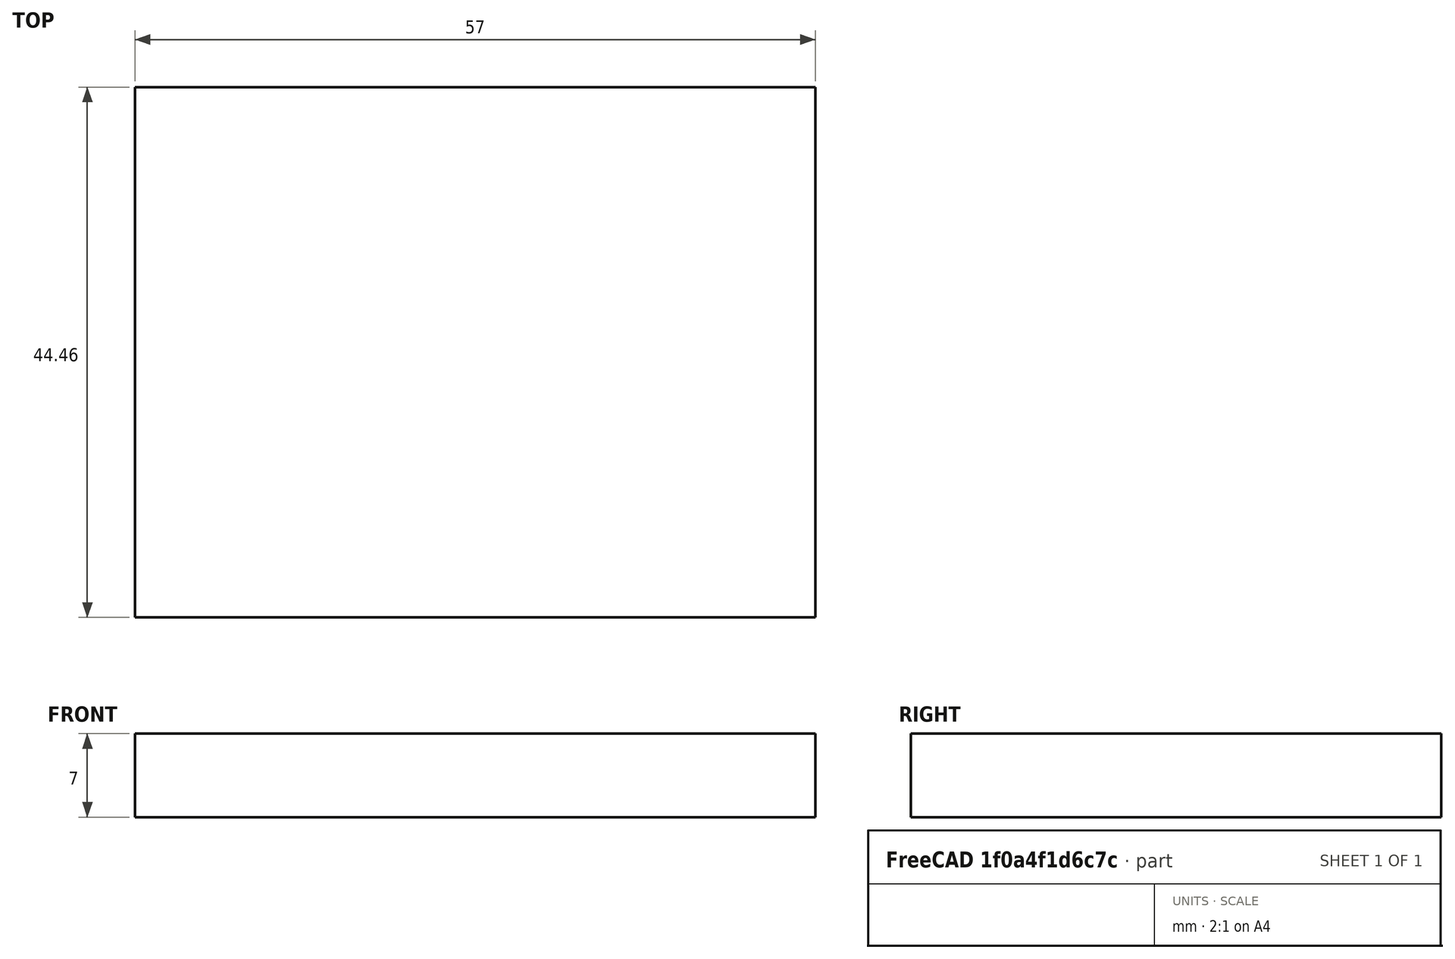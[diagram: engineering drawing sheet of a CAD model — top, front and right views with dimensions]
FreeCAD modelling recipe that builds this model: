
FCSTD DOCUMENT  (FreeCAD 0.17RUnknown)
Label: cam_cage
License: All rights reserved
LicenseURL: http://en.wikipedia.org/wiki/All_rights_reserved
objects: Path::FeaturePython×8, Part::FeaturePython×3, App::FeaturePython×1, Path::FeatureCompoundPython×1
note: 6 computed .brp shape members not serialized (recipe doc carries the construction recipe); baked Part::Feature solids carry a one-line shape summary decoded from their .brp

FEATURE [Path::FeaturePython] Default_Tool  label="Default Tool"  # Path/CAM operation (typed FeaturePython)
  HorizFeed = 3.33333
  HorizRapid = 0
  SpindleDir = 0
  SpindleSpeed = 24000
  ToolNumber = 1
  VertFeed = 0.666667
  VertRapid = 0
  expr: Tool.Diameter = 2
  expr: VertFeed = 40mm / min
  expr: HorizFeed = 200mm / min
  expr: HorizRapid = SetupSheet.HorizRapid
  expr: VertRapid = SetupSheet.VertRapid
FEATURE [Path::FeaturePython] Contour  # Path/CAM operation (typed FeaturePython)
  Active = true
  AreaParams:
    OpenMode = 0
    Angle = 45.0
    MinArcPoints = 4
    Coplanar = 2
    Tolerance = 1e-07
    CleanDistance = 0.0
    PocketExtraOffset = 0.0
    RoundPrecision = 0.0
    AngleShift = 0.0
    SubjectFill = 0
    PocketMode = 0
    Simplify = False
    SectionTolerance = 1e-06
    MaxArcPoints = 100
    Offset = 1.0
    Accuracy = 0.01
    PocketStepover = 0.0
    ClipFill = 0
    ToolRadius = 1.0
    Outline = False
    ClipperScale = 10000000.0
    FromCenter = False
    Explode = False
    EndType = 0
    Shift = 0.0
    ExtraPass = 0
    Project = False
    JoinType = 0
    Thicken = False
    Stepdown = 1.0
    SectionMode = 2
    MiterLimit = 2.0
    Deflection = 0.01
    Reorient = True
    FitArcs = True
    SectionCount = -1
    SectionOffset = 0.0
    Stepover = 0.0
    Unit = 1.0
    Fill = 0
  ClearanceHeight = 2
  Direction = 0
  FinalDepth = -5.5
  JoinType = 0
  MiterLimit = 0.1
  OffsetExtra = 0
  OpFinalDepth = -6
  OpStartDepth = 1
  OpToolDiameter = 2
  PathParams = {'resume_height': 2.0, 'feedrate': 3.3333333333333335, 'verbose': True, 'orientation': 1, 'return_end': True, 'preamble': False, 'retraction': 2.0, 'feedrate_v': 0.6666666666666666}
  SafeHeight = 2
  Side = 0
  StartDepth = 0
  StartPoint = (0,0,0)
  StepDown = 0.1
  ToolController = -> Default_Tool
  UseComp = true
  UseStartPoint = false
  expr: FinalDepth = -5.5
  expr: ClearanceHeight = StartDepth + SetupSheet.ClearanceHeightOffset
  expr: SafeHeight = StartDepth + SetupSheet.SafeHeightOffset
  expr: StepDown = 0.10000000000000001
  expr: StartDepth = 0
FEATURE [App::FeaturePython] SetupSheet  # Path/CAM operation (typed FeaturePython)
  ClearanceHeightExpression = StartDepth+SetupSheet.ClearanceHeightOffset
  ClearanceHeightOffset = 2
  FinalDepthExpression = OpFinalDepth
  HorizRapid = 0
  SafeHeightExpression = StartDepth+SetupSheet.SafeHeightOffset
  SafeHeightOffset = 2
  StartDepthExpression = OpStartDepth
  StepDownExpression = OpToolDiameter
  VertRapid = 0
FEATURE [Part::FeaturePython] cage_01  # a2plus imported part (geometry in sourceFile) (typed FeaturePython)
  Placement = pos=(-28.7964,26.9328,-28.4564) rot=(0.57735,0.57735,0.57735;0rad)
  fixedPosition = false
  sourceFile = <userpath>/hs/fly/cad/cage.fcstd
  timeLastImport = 1.53702e+09
  updateColors = true
FEATURE [Part::FeaturePython] Clone  label="Base-arm_01"  # Draft clone (typed FeaturePython)
  AttacherType = Attacher::AttachEngine3D
  Fuse = false
  Objects = -> [cage_01]
  PathResource = Base
  Placement = pos=(51,12,-2.5) rot=(-1,0,0;0rad)
  Scale = (1,1,1)
FEATURE [Part::FeaturePython] Stock  # WARN: FeaturePython — macro-defined, semantics opaque (R4)
  Base = -> Clone
  ExtXneg = 1
  ExtXpos = 1
  ExtYneg = 1
  ExtYpos = 1
  ExtZneg = 1
  ExtZpos = 1
  StockType = FromBase
FEATURE [Path::FeaturePython] Pocket_Shape001  # Path/CAM operation (typed FeaturePython)
  Active = true
  AreaParams:
    OpenMode = 0
    Angle = 45.0
    MinArcPoints = 4
    Coplanar = 0
    Tolerance = 1e-07
    CleanDistance = 0.0
    PocketExtraOffset = 0.0
    RoundPrecision = 0.0
    AngleShift = 0.0
    SubjectFill = 0
    PocketMode = 2
    Simplify = False
    SectionTolerance = 1e-06
    MaxArcPoints = 100
    Offset = 0.0
    Accuracy = 0.01
    PocketStepover = 1.0
    ClipFill = 0
    ToolRadius = 1.0
    Outline = False
    ClipperScale = 10000000.0
    FromCenter = True
    Explode = False
    EndType = 0
    Shift = 0.0
    ExtraPass = 0
    Project = False
    JoinType = 0
    Thicken = False
    Stepdown = 1.0
    SectionMode = 2
    MiterLimit = 2.0
    Deflection = 0.01
    Reorient = True
    FitArcs = True
    SectionCount = -1
    SectionOffset = 0.0
    Stepover = 0.0
    Unit = 1.0
    Fill = 0
  Base = -> [Clone]
  ClearanceHeight = 2
  CutMode = 0
  ExtraOffset = 0
  FinalDepth = -5.5
  FinishDepth = 0
  KeepToolDown = false
  MinTravel = false
  OffsetPattern = 1
  OpFinalDepth = -5
  OpStartDepth = 1
  OpToolDiameter = 2
  PathParams = {'resume_height': 2.0, 'feedrate': 3.3333333333333335, 'verbose': True, 'orientation': 1, 'return_end': True, 'preamble': False, 'retraction': 2.0, 'feedrate_v': 0.6666666666666666}
  SafeHeight = 2
  StartAt = 0
  StartDepth = 0
  StartPoint = (0,0,0)
  StepDown = 0.21
  StepOver = 50
  ToolController = -> Default_Tool
  UseStartPoint = false
  ZigZagAngle = 45
  expr: ClearanceHeight = StartDepth + SetupSheet.ClearanceHeightOffset
  expr: SafeHeight = StartDepth + SetupSheet.SafeHeightOffset
  expr: StepDown = 0.20999999999999999
  expr: FinalDepth = -5.5
  expr: StartDepth = 0
FEATURE [Path::FeaturePython] Drilling  # Path/CAM operation (typed FeaturePython)
  Active = true
  AddTipLength = false
  Base = -> [Clone]
  ClearanceHeight = 3
  Disabled = Clone.Face44 | Clone.Face45
  DwellEnabled = false
  DwellTime = 0
  FinalDepth = -0.2
  OpFinalDepth = -5
  OpStartDepth = 1
  OpToolDiameter = 2
  PeckDepth = 0
  PeckEnabled = false
  RetractHeight = 10
  ReturnLevel = 0
  SafeHeight = 3
  StartDepth = 1
  ToolController = -> Default_Tool
  expr: ClearanceHeight = StartDepth + SetupSheet.ClearanceHeightOffset
  expr: SafeHeight = StartDepth + SetupSheet.SafeHeightOffset
  expr: FinalDepth = -0.20000000000000001
  expr: StartDepth = OpStartDepth
FEATURE [Path::FeaturePython] Profile_Edges  # Path/CAM operation (typed FeaturePython)
  Active = true
  AreaParams:
    OpenMode = 0
    Angle = 45.0
    MinArcPoints = 4
    Coplanar = 0
    Tolerance = 1e-07
    CleanDistance = 0.0
    PocketExtraOffset = 0.0
    RoundPrecision = 0.0
    AngleShift = 0.0
    SubjectFill = 0
    PocketMode = 0
    Simplify = False
    SectionTolerance = 1e-06
    MaxArcPoints = 100
    Offset = -1.0
    Accuracy = 0.01
    PocketStepover = 0.0
    ClipFill = 0
    ToolRadius = 1.0
    Outline = False
    ClipperScale = 10000000.0
    FromCenter = False
    Explode = False
    EndType = 0
    Shift = 0.0
    ExtraPass = 0
    Project = False
    JoinType = 0
    Thicken = False
    Stepdown = 1.0
    SectionMode = 2
    MiterLimit = 2.0
    Deflection = 0.01
    Reorient = True
    FitArcs = True
    SectionCount = -1
    SectionOffset = 0.0
    Stepover = 0.0
    Unit = 1.0
    Fill = 0
  Base = -> [Clone]
  ClearanceHeight = 2
  Direction = 0
  FinalDepth = -5.5
  JoinType = 0
  MiterLimit = 0.1
  OffsetExtra = 0
  OpFinalDepth = -5
  OpStartDepth = 1
  OpToolDiameter = 2
  PathParams = {'resume_height': 2.0, 'feedrate': 3.3333333333333335, 'verbose': True, 'orientation': 1, 'return_end': True, 'preamble': False, 'retraction': 2.0, 'feedrate_v': 0.6666666666666666}
  SafeHeight = 2
  Side = 1
  StartDepth = 0
  StartPoint = (0,0,0)
  StepDown = 0.1
  ToolController = -> Default_Tool
  UseComp = true
  UseStartPoint = false
  expr: ClearanceHeight = StartDepth + SetupSheet.ClearanceHeightOffset
  expr: SafeHeight = StartDepth + SetupSheet.SafeHeightOffset
  expr: StepDown = 0.10000000000000001
  expr: FinalDepth = -5.5
  expr: StartDepth = 0
FEATURE [Path::FeaturePython] TagDressup  # Path/CAM operation (typed FeaturePython)
  Angle = 45
  Base = -> Profile_Edges
  Height = 3
  Positions = (4) [(27.27,17.45,0),(7,21.12,0),(35.69,18.63,0),(45,10.2,0)]
  Radius = 0
  SegmentationFactor = 50
  Width = 3.8
FEATURE [Path::FeaturePython] TagDressup001  # Path/CAM operation (typed FeaturePython)
  Angle = 45
  Base = -> Contour
  Height = 2.75
  Positions = (4) [(57,12,-5.5),(33.2598,33.4653,-5.5),(27.0808,2.32053,-5.5),(0.000541454,21.2218,-5.5)]
  Radius = 0
  SegmentationFactor = 50
  Width = 3.80694
FEATURE [Path::FeatureCompoundPython] Operations  # Path/CAM operation (typed FeaturePython)
  Group = -> [Drilling,Pocket_Shape001,TagDressup,TagDressup001]
  UsePlacements = false
FEATURE [Path::FeaturePython] Job  # Path/CAM operation (typed FeaturePython)
  Base = -> Clone
  GeometryTolerance = 0.01
  Operations = -> Operations
  PostProcessor = 5
  PostProcessorOutputFile = <userpath>/hs/fly/cad/gcode/arm
  SetupSheet = -> SetupSheet
  Stock = -> Stock
  ToolController = -> [Default_Tool]
